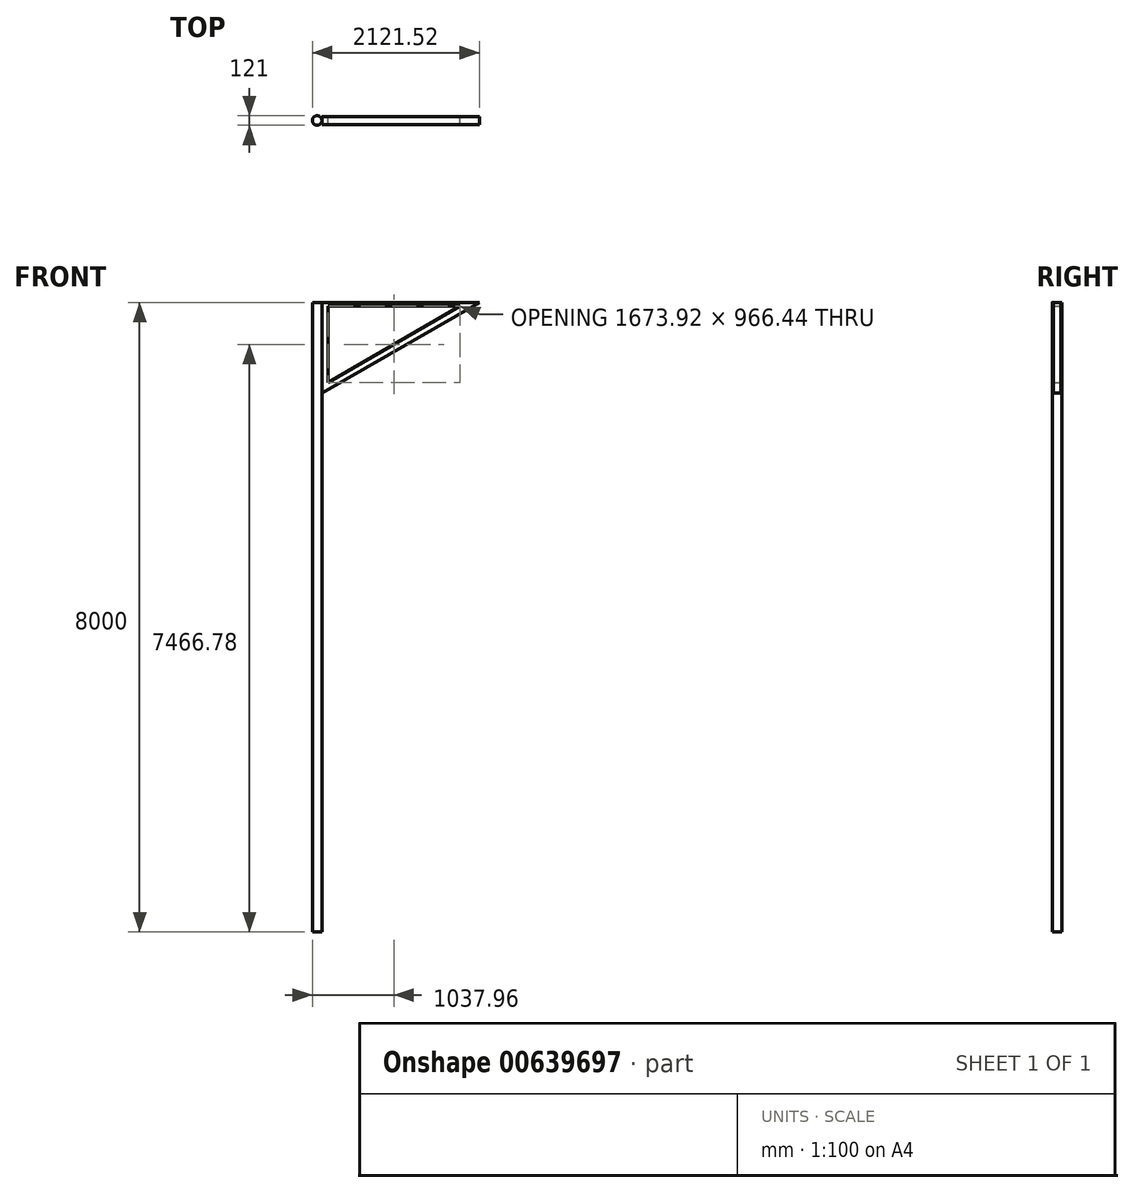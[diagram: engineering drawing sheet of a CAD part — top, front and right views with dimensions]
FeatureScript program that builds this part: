
annotation { "Feature Type Name" : "Feature", "Feature Type Description" : "" }
export const myFeature = defineFeature(function(context is Context, id is Id, definition is map)
    precondition{}
    {
        {
            var Q0;
            Q0=qCreatedBy(makeId("Top.planeOp"),FACE);
            var sketch = newSketch(context, id + "F0", { "sketchPlane" : qUnion([Q0])});
            skCircle(sketch, "E0", {"center": v(0, 0) * mm, "radius": 60.5 * mm});
            skSolve(sketch);
        }
        {
            var Q0;
            Q0=qSketchRegion(id+"F0",true);
            extrude(context, id + "F1", {"entities" : qUnion([Q0]), "depth" : 8000 * mm, "offsetDistance" : 25 * mm});
        }
        {
            var Q0;
            Q0=qCreatedBy(makeId("Front.planeOp"),FACE);
            var sketch = newSketch(context, id + "F2", { "sketchPlane" : qUnion([Q0])});
            skLineSegment(sketch, "E1", {"start": v(60.5, 8000) * mm, "end": v(60.5, 6845) * mm});
            skLineSegment(sketch, "E2", {"start": v(60.5, 6845) * mm, "end": v(2061.02, 8000) * mm});
            skLineSegment(sketch, "E3", {"start": v(2061.02, 8000) * mm, "end": v(60.5, 8000) * mm});
            skLineSegment(sketch, "E4", {"start": v(60.5, 8000) * mm, "end": v(60.5, 0) * mm, "construction": true});
            skLineSegment(sketch, "E5", {"start": v(-60.5, 0) * mm, "end": v(-60.5, 8000) * mm});
            skLineSegment(sketch, "E6", {"start": v(140.5, 7950) * mm, "end": v(140.5, 6983.56) * mm});
            skLineSegment(sketch, "E7", {"start": v(140.5, 6983.56) * mm, "end": v(1814.42, 7950) * mm});
            skLineSegment(sketch, "E8", {"start": v(1814.42, 7950) * mm, "end": v(140.5, 7950) * mm});
            skSolve(sketch);
        }
        {
            var Q0;
            Q0=qSketchRegion(id+"F2",true);
            extrude(context, id + "F3", {"entities" : qUnion([Q0]), "operationType" : NewBodyOperationType.ADD, "endBound" : BoundingType.SYMMETRIC, "depth" : 100 * mm, "offsetDistance" : 25 * mm});
        }
    });
